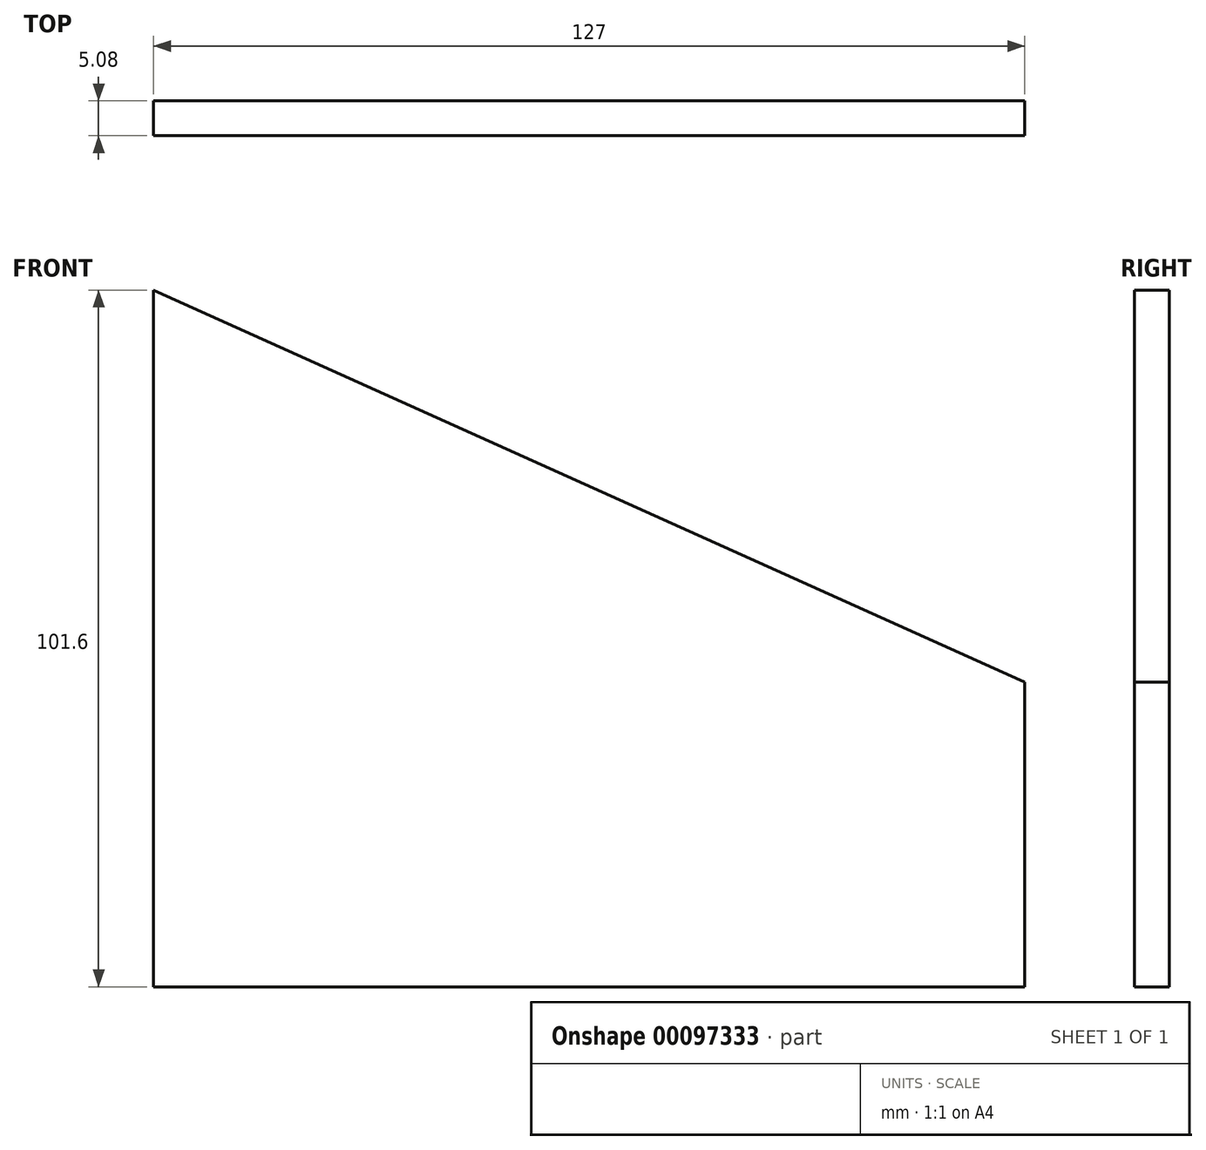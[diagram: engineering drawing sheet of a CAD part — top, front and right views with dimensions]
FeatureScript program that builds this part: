
annotation { "Feature Type Name" : "Feature", "Feature Type Description" : "" }
export const myFeature = defineFeature(function(context is Context, id is Id, definition is map)
    precondition{}
    {
        {
            var Q0;
            Q0=qCreatedBy(makeId("Front.planeOp"),FACE);
            var sketch = newSketch(context, id + "F0", { "sketchPlane" : qUnion([Q0])});
            skLineSegment(sketch, "E0", {"start": v(-42.41, 40.72) * mm, "end": v(-42.41, -60.88) * mm});
            skLineSegment(sketch, "E1", {"start": v(-42.41, -60.88) * mm, "end": v(84.59, -60.88) * mm});
            skLineSegment(sketch, "E2", {"start": v(84.59, -60.88) * mm, "end": v(84.59, -16.45) * mm});
            skLineSegment(sketch, "E3", {"start": v(84.59, -16.45) * mm, "end": v(-42.41, 40.72) * mm});
            skSolve(sketch);
        }
        {
            var Q0;
            Q0=makeQuery(id+"F0.imprint","IMPRINT",FACE,{"disambiguationData":[TD([[makeQuery(id+"F0.imprint","IMPRINT",EDGE,{"derivedFrom":sQuery(id+"F0.wireOp",EDGE,"E0")}),1.0]])]});
            extrude(context, id + "F1", {"entities" : qUnion([Q0]), "depth" : 5.08 * mm});
        }
    });
